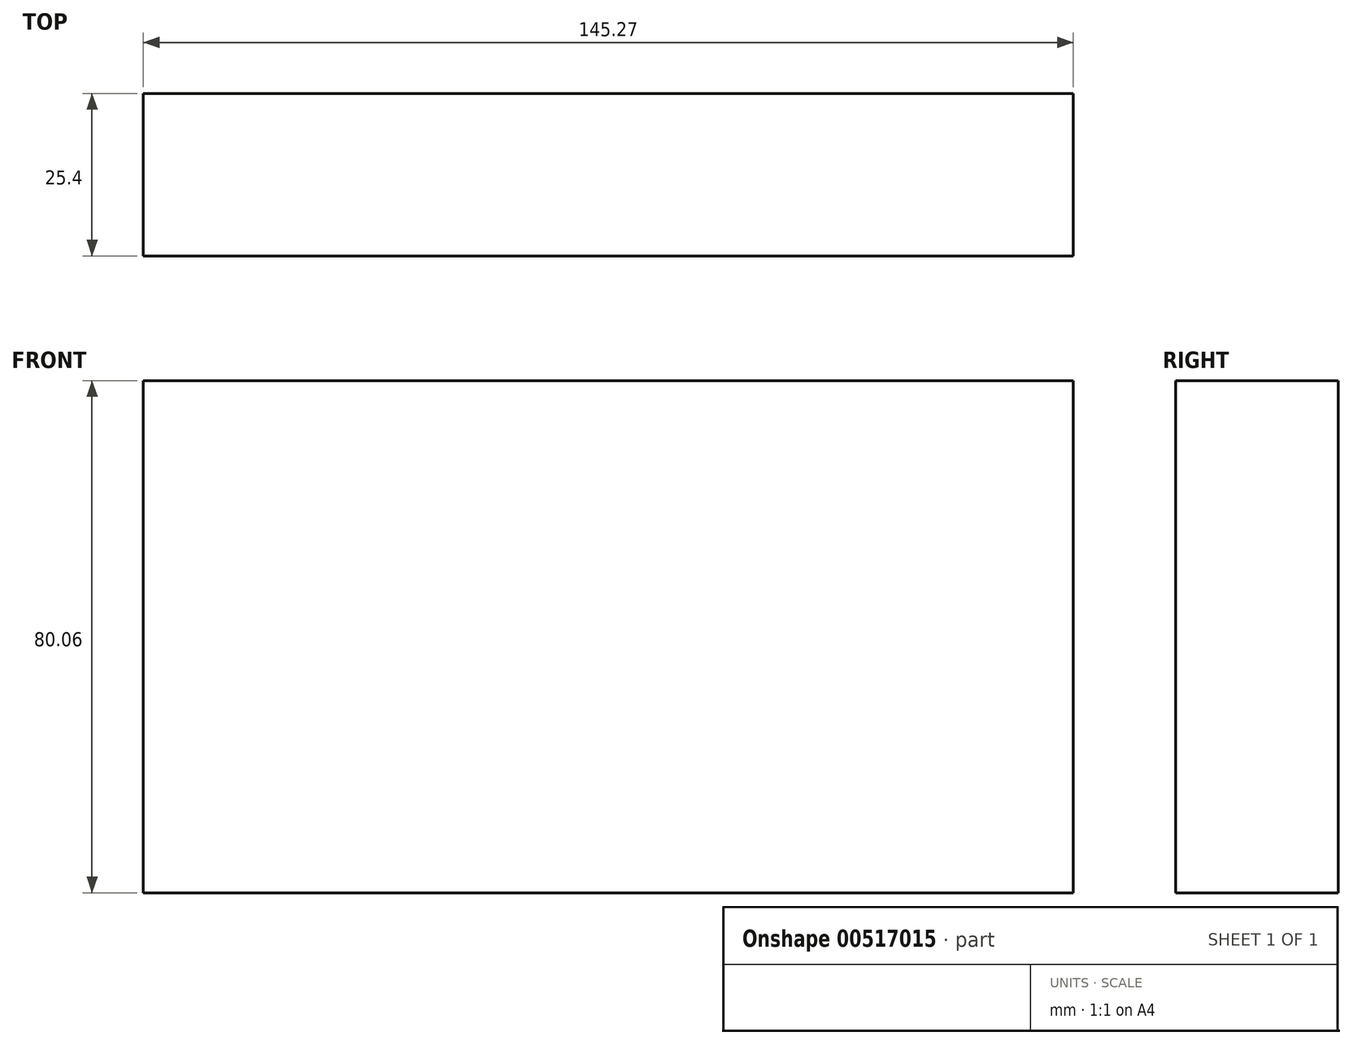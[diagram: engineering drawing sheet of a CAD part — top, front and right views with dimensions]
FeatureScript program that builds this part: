
annotation { "Feature Type Name" : "Feature", "Feature Type Description" : "" }
export const myFeature = defineFeature(function(context is Context, id is Id, definition is map)
    precondition{}
    {
        {
            var Q0;
            Q0=qCreatedBy(makeId("Front.planeOp"),FACE);
            var sketch = newSketch(context, id + "F0", { "sketchPlane" : qUnion([Q0])});
            skLineSegment(sketch, "E0.bottom", {"start": v(-98.93, 49.68) * mm, "end": v(46.34, 49.68) * mm});
            skLineSegment(sketch, "E0.top", {"start": v(-98.93, -30.38) * mm, "end": v(46.34, -30.38) * mm});
            skLineSegment(sketch, "E0.left", {"start": v(-98.93, 49.68) * mm, "end": v(-98.93, -30.38) * mm});
            skLineSegment(sketch, "E0.right", {"start": v(46.34, 49.68) * mm, "end": v(46.34, -30.38) * mm});
            skSolve(sketch);
        }
        {
            var Q0;
            Q0 = qSketchRegion(id + "F0", true);
            extrude(context, id + "F1", {"entities" : qUnion([Q0]), "depth" : 25.4 * mm, "offsetDistance" : 25.4 * mm});
        }
    });
